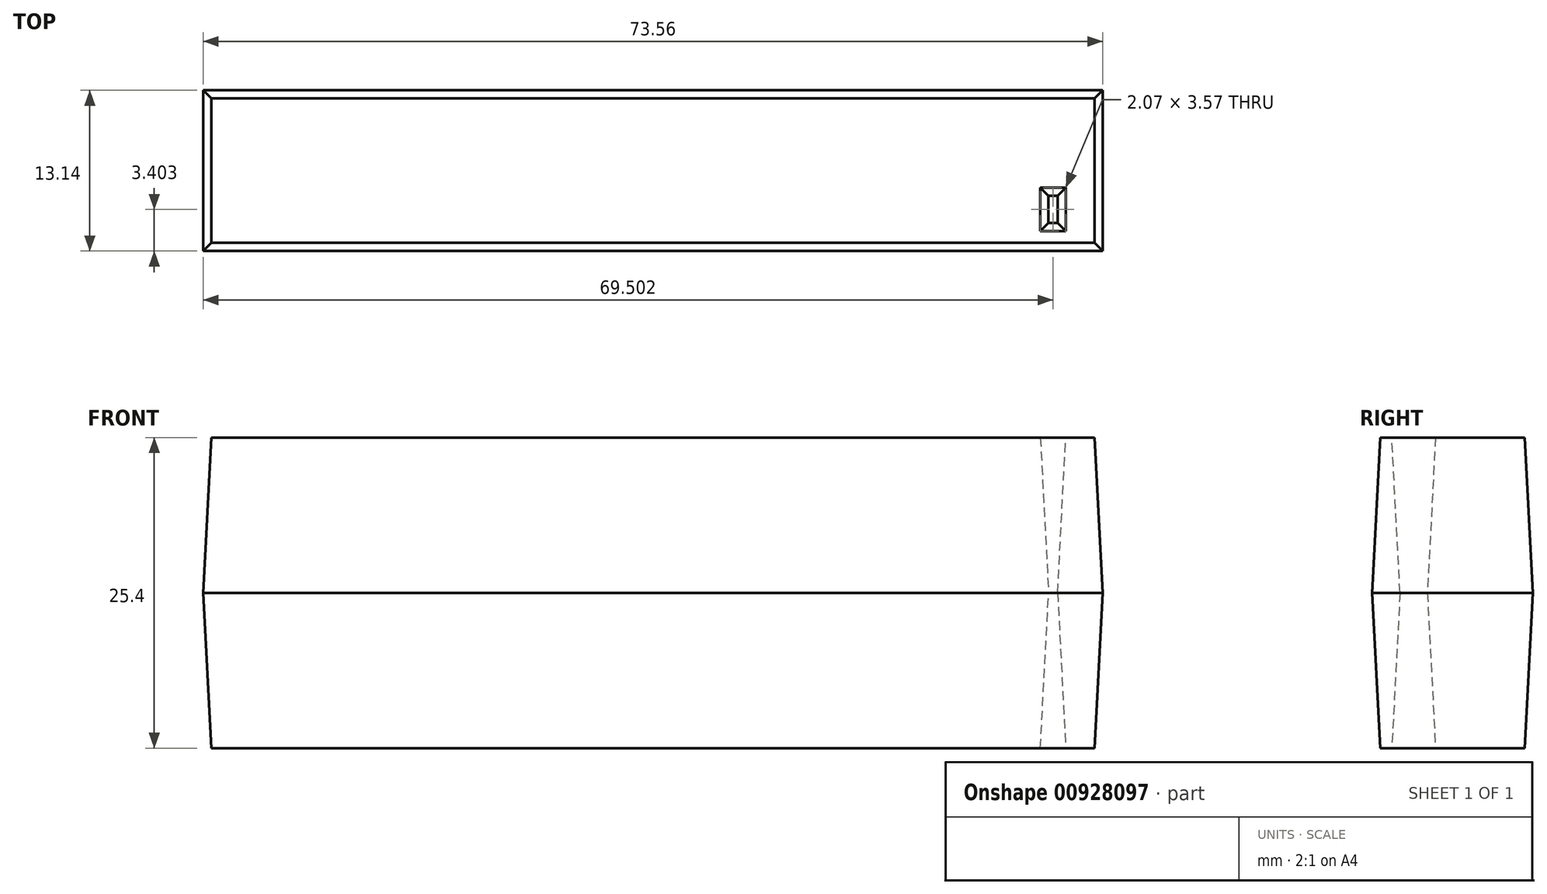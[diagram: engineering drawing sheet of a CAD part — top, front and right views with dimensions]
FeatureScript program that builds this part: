
annotation { "Feature Type Name" : "Feature", "Feature Type Description" : "" }
export const myFeature = defineFeature(function(context is Context, id is Id, definition is map)
    precondition{}
    {
        {
            var Q0;
            Q0=qCreatedBy(makeId("Top.planeOp"),FACE);
            var sketch = newSketch(context, id + "F0", { "sketchPlane" : qUnion([Q0])});
            skLineSegment(sketch, "E0.bottom", {"start": v(73.56, 61.82) * mm, "end": v(65.84, 61.82) * mm});
            skLineSegment(sketch, "E0.top", {"start": v(73.56, 58.2) * mm, "end": v(65.84, 58.2) * mm});
            skLineSegment(sketch, "E0.left", {"start": v(73.56, 61.82) * mm, "end": v(73.56, 58.2) * mm});
            skLineSegment(sketch, "E0.right", {"start": v(65.84, 61.82) * mm, "end": v(65.84, 58.2) * mm});
            skLineSegment(sketch, "E1.bottom", {"start": v(73.56, 61.82) * mm, "end": v(0, 61.82) * mm});
            skLineSegment(sketch, "E1.top", {"start": v(73.56, 74.96) * mm, "end": v(0, 74.96) * mm});
            skLineSegment(sketch, "E1.left", {"start": v(73.56, 61.82) * mm, "end": v(73.56, 74.96) * mm});
            skLineSegment(sketch, "E1.right", {"start": v(0, 61.82) * mm, "end": v(0, 74.96) * mm});
            skLineSegment(sketch, "E2.bottom", {"start": v(0, 0) * mm, "end": v(75.54, 0) * mm});
            skLineSegment(sketch, "E2.top", {"start": v(0, -75.15) * mm, "end": v(75.54, -75.15) * mm});
            skLineSegment(sketch, "E2.left", {"start": v(0, 0) * mm, "end": v(0, -75.15) * mm});
            skLineSegment(sketch, "E2.right", {"start": v(75.54, 0) * mm, "end": v(75.54, -75.15) * mm});
            skLineSegment(sketch, "E3.bottom", {"start": v(0, 0) * mm, "end": v(-75.1, 0) * mm});
            skLineSegment(sketch, "E3.top", {"start": v(0, -75.2) * mm, "end": v(-75.1, -75.2) * mm});
            skLineSegment(sketch, "E3.left", {"start": v(0, 0) * mm, "end": v(0, -75.2) * mm});
            skLineSegment(sketch, "E3.right", {"start": v(-75.1, 0) * mm, "end": v(-75.1, -75.2) * mm});
            skLineSegment(sketch, "E4.bottom", {"start": v(0, 61.82) * mm, "end": v(0, 61.82) * mm});
            skLineSegment(sketch, "E4.top", {"start": v(0, 0) * mm, "end": v(0, 0) * mm});
            skLineSegment(sketch, "E4.left", {"start": v(0, 61.82) * mm, "end": v(0, 0) * mm});
            skLineSegment(sketch, "E4.right", {"start": v(0, 61.82) * mm, "end": v(0, 0) * mm});
            skLineSegment(sketch, "E5.bottom", {"start": v(81.47, 58.2) * mm, "end": v(73.56, 58.2) * mm});
            skLineSegment(sketch, "E5.top", {"start": v(81.47, 74.96) * mm, "end": v(73.56, 74.96) * mm});
            skLineSegment(sketch, "E5.left", {"start": v(81.47, 58.2) * mm, "end": v(81.47, 74.96) * mm});
            skLineSegment(sketch, "E5.right", {"start": v(73.56, 58.2) * mm, "end": v(73.56, 74.96) * mm});
            skLineSegment(sketch, "E6.bottom", {"start": v(74.65, 64.79) * mm, "end": v(81.47, 64.79) * mm});
            skLineSegment(sketch, "E6.top", {"start": v(74.65, 74.96) * mm, "end": v(81.47, 74.96) * mm});
            skLineSegment(sketch, "E6.left", {"start": v(74.65, 64.79) * mm, "end": v(74.65, 74.96) * mm});
            skLineSegment(sketch, "E6.right", {"start": v(81.47, 64.79) * mm, "end": v(81.47, 74.96) * mm});
            skLineSegment(sketch, "E7.bottom", {"start": v(95.04, 141.98) * mm, "end": v(75.7, 141.98) * mm});
            skLineSegment(sketch, "E7.top", {"start": v(95.04, 88.97) * mm, "end": v(75.7, 88.97) * mm});
            skLineSegment(sketch, "E7.left", {"start": v(95.04, 141.98) * mm, "end": v(95.04, 88.97) * mm});
            skLineSegment(sketch, "E7.right", {"start": v(75.7, 141.98) * mm, "end": v(75.7, 88.97) * mm});
            skLineSegment(sketch, "E8.bottom", {"start": v(74.67, 58.09) * mm, "end": v(65.84, 58.09) * mm});
            skLineSegment(sketch, "E8.top", {"start": v(74.67, 61.82) * mm, "end": v(65.84, 61.82) * mm});
            skLineSegment(sketch, "E8.left", {"start": v(74.67, 58.09) * mm, "end": v(74.67, 61.82) * mm});
            skLineSegment(sketch, "E8.right", {"start": v(65.84, 58.09) * mm, "end": v(65.84, 61.82) * mm});
            skLineSegment(sketch, "E9.bottom", {"start": v(69.87, 64.1) * mm, "end": v(69.13, 64.1) * mm});
            skLineSegment(sketch, "E9.top", {"start": v(69.87, 66.34) * mm, "end": v(69.13, 66.34) * mm});
            skLineSegment(sketch, "E9.left", {"start": v(69.87, 64.1) * mm, "end": v(69.87, 66.34) * mm});
            skLineSegment(sketch, "E9.right", {"start": v(69.13, 64.1) * mm, "end": v(69.13, 66.34) * mm});
            skSolve(sketch);
        }
        {
            var Q0;
            {var subQ4=sQuery(id+"F0.wireOp",EDGE,"E1.bottom");Q0=makeQuery(id+"F0.imprint","IMPRINT",FACE,{"disambiguationData":[TD([[makeQuery(id+"F0.imprint","IMPRINT",EDGE,{"derivedFrom":subQ4}),-1.0]])]});}
            extrude(context, id + "F1", {"entities" : qUnion([Q0]), "endBound" : BoundingType.SYMMETRIC, "depth" : 25.4 * mm, "offsetDistance" : 25.4 * mm, "hasDraft" : true, "draftAngle" : 3 * degree, "draftPullDirection" : true});
        }
    });
